# Revit family: Toilet_Holder-Grohe-Essentials-40367_Series
name_source: partatom
category: Specialty Equipment
units: mm (PartAtom-declared; Revit-internal decimal feet)

## family parameters
Cut with Voids When Loaded = No
Host = Face
OmniClass Number = 23.40.20.21.21
OmniClass Title = Toilet Paper Dispensers
Part Type = Normal
Room Calculation Point = No
Round Connector Dimension = Use Diameter
Shared = Yes

## types (2) — shared parameters
Assembly Code = C1030200
Default Elevation = 16"
Description = Essentials Toilet Paper Holder
Height = 2 1/8"
Installation Type = Wall Mounted
Length = 6 5/8"
Manufacturer = Grohe
Price = Prices may vary. Please consult Manufacturer Representative for most up-to-date price list.
Product Documentation Link = https://americanstandard.box.com
URL = https://www.grohe.us
Width = 1 3/4"

## per-type parameters (varying)
| type | Finish | Material | Product Page URL |
| 40367001 | Metal-Grohe-001-StarLight Chrome | Metal-Grohe-001-StarLight Chrome | https://www.grohe.us |
| 40367EN1 | Metal-Grohe-EN0-Brushed Nickel | Metal-Grohe-EN0-Brushed Nickel | https://www.grohe.ca |

note: column(s) folded — value = type name in every type: Model

## geometry (parser evidence)
native form markers: Sweep x4
no freeform markers — native parametric forms only
